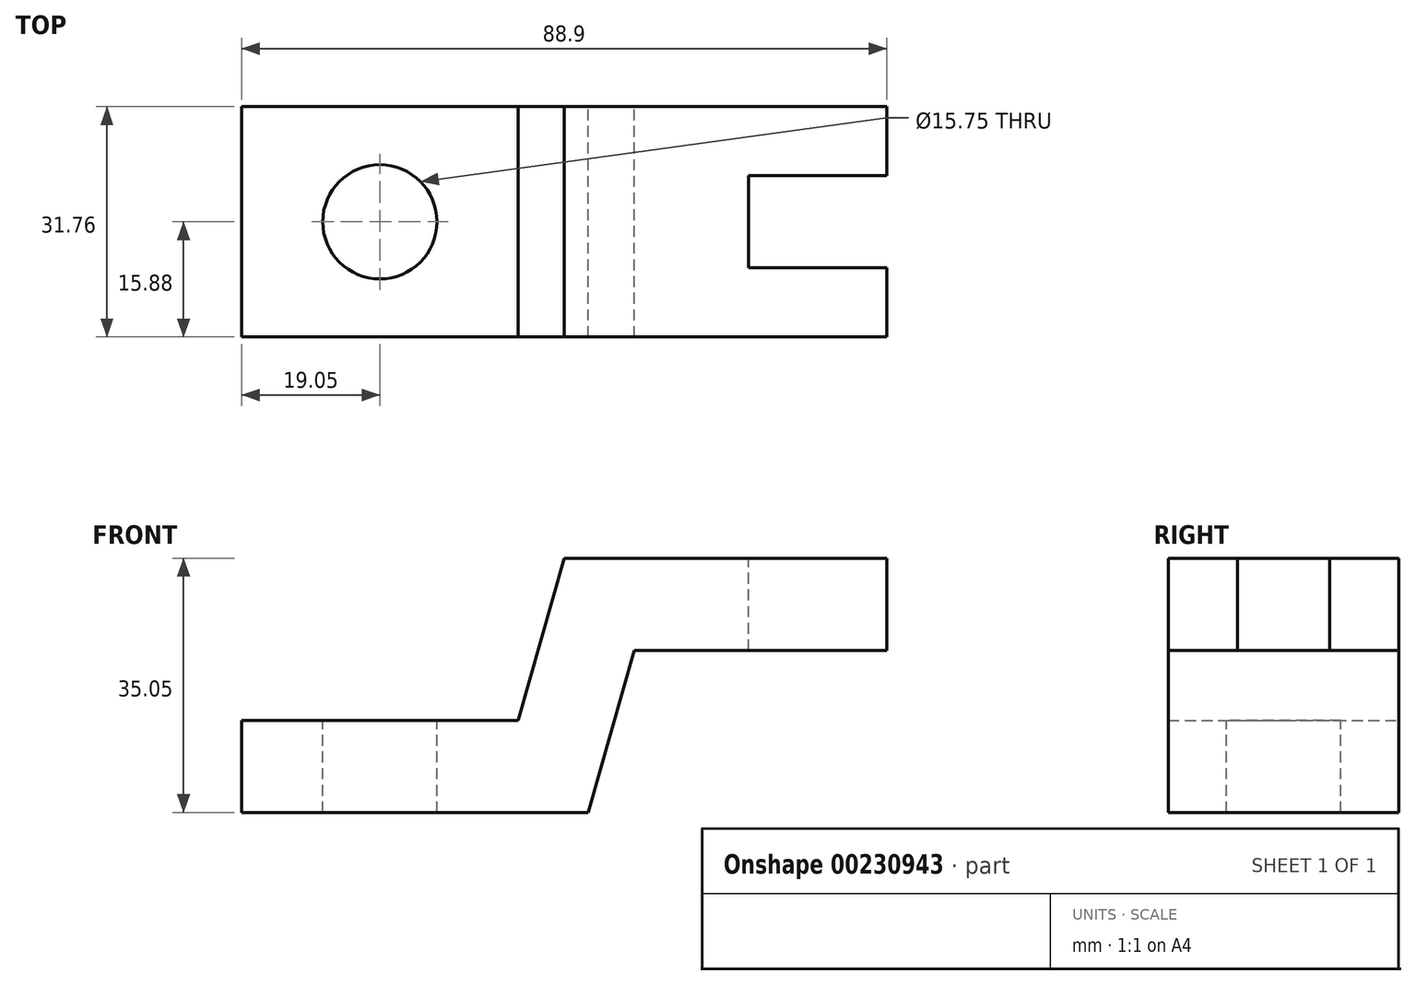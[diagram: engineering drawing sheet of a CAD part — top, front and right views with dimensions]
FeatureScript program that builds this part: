
annotation { "Feature Type Name" : "Feature", "Feature Type Description" : "" }
export const myFeature = defineFeature(function(context is Context, id is Id, definition is map)
    precondition{}
    {
        {
            var Q0;
            Q0=qCreatedBy(makeId("Front.planeOp"),FACE);
            var sketch = newSketch(context, id + "F0", { "sketchPlane" : qUnion([Q0])});
            skLineSegment(sketch, "E0", {"start": v(0, 0) * mm, "end": v(47.75, 0) * mm});
            skLineSegment(sketch, "E1", {"start": v(88.9, 22.35) * mm, "end": v(88.9, 35.05) * mm});
            skLineSegment(sketch, "E2", {"start": v(88.9, 35.05) * mm, "end": v(88.9, 22.35) * mm});
            skLineSegment(sketch, "E3", {"start": v(88.9, 22.35) * mm, "end": v(54.1, 22.35) * mm});
            skLineSegment(sketch, "E4", {"start": v(47.75, 0) * mm, "end": v(54.1, 22.35) * mm});
            skLineSegment(sketch, "E5", {"start": v(88.9, 35.05) * mm, "end": v(44.45, 35.05) * mm});
            skLineSegment(sketch, "E6", {"start": v(0, 0) * mm, "end": v(0, 12.7) * mm});
            skLineSegment(sketch, "E7", {"start": v(0, 12.7) * mm, "end": v(38.1, 12.7) * mm});
            skLineSegment(sketch, "E8", {"start": v(38.1, 12.7) * mm, "end": v(44.45, 35.05) * mm});
            skSolve(sketch);
        }
        {
            var Q0;
            Q0=makeQuery(id+"F0.imprint","IMPRINT",FACE,{"disambiguationData":[TD([[makeQuery(id+"F0.imprint","IMPRINT",EDGE,{"derivedFrom":sQuery(id+"F0.wireOp",EDGE,"E0")}),1.0]])]});
            extrude(context, id + "F1", {"entities" : qUnion([Q0]), "endBound" : BoundingType.SYMMETRIC, "depth" : 31.75 * mm});
        }
        {
            var Q0;
            Q0=makeQuery(id+"F1.opExtrude","SWEPT_FACE",FACE,{"disambiguationData":[OSD([sQuery(id+"F0.wireOp",EDGE,"E5")])]});
            var sketch = newSketch(context, id + "F2", { "sketchPlane" : qUnion([Q0])});
            skLineSegment(sketch, "E9", {"start": v(88.9, 6.35) * mm, "end": v(69.85, 6.35) * mm});
            skLineSegment(sketch, "E10", {"start": v(88.9, -6.35) * mm, "end": v(69.85, -6.35) * mm});
            skLineSegment(sketch, "E11", {"start": v(69.85, -6.35) * mm, "end": v(69.85, 6.35) * mm});
            skLineSegment(sketch, "E12", {"start": v(88.9, 6.35) * mm, "end": v(88.9, -6.35) * mm});
            skSolve(sketch);
        }
        {
            var Q0;
            Q0=makeQuery(id+"F2.imprint","IMPRINT",FACE,{"disambiguationData":[TD([[makeQuery(id+"F2.imprint","IMPRINT",EDGE,{"derivedFrom":sQuery(id+"F2.wireOp",EDGE,"E9")}),1.0]])]});
            extrude(context, id + "F3", {"entities" : qUnion([Q0]), "operationType" : NewBodyOperationType.REMOVE, "oppositeDirection" : true, "depth" : 25.4 * mm});
        }
        {
            var Q0;
            Q0=makeQuery(id+"F1.opExtrude","SWEPT_FACE",FACE,{"disambiguationData":[OSD([sQuery(id+"F0.wireOp",EDGE,"E7")])]});
            var sketch = newSketch(context, id + "F4", { "sketchPlane" : qUnion([Q0])});
            skCircle(sketch, "E13", {"center": v(19.05, 0) * mm, "radius": 7.87 * mm});
            skSolve(sketch);
        }
        {
            var Q0;
            Q0=makeQuery(id+"F4.imprint","IMPRINT",FACE,{"disambiguationData":[TD([[makeQuery(id+"F4.imprint","IMPRINT",EDGE,{"derivedFrom":sQuery(id+"F4.wireOp",EDGE,"E13")}),1.0]])]});
            extrude(context, id + "F5", {"entities" : qUnion([Q0]), "operationType" : NewBodyOperationType.REMOVE, "oppositeDirection" : true, "depth" : 25.4 * mm});
        }
    });
